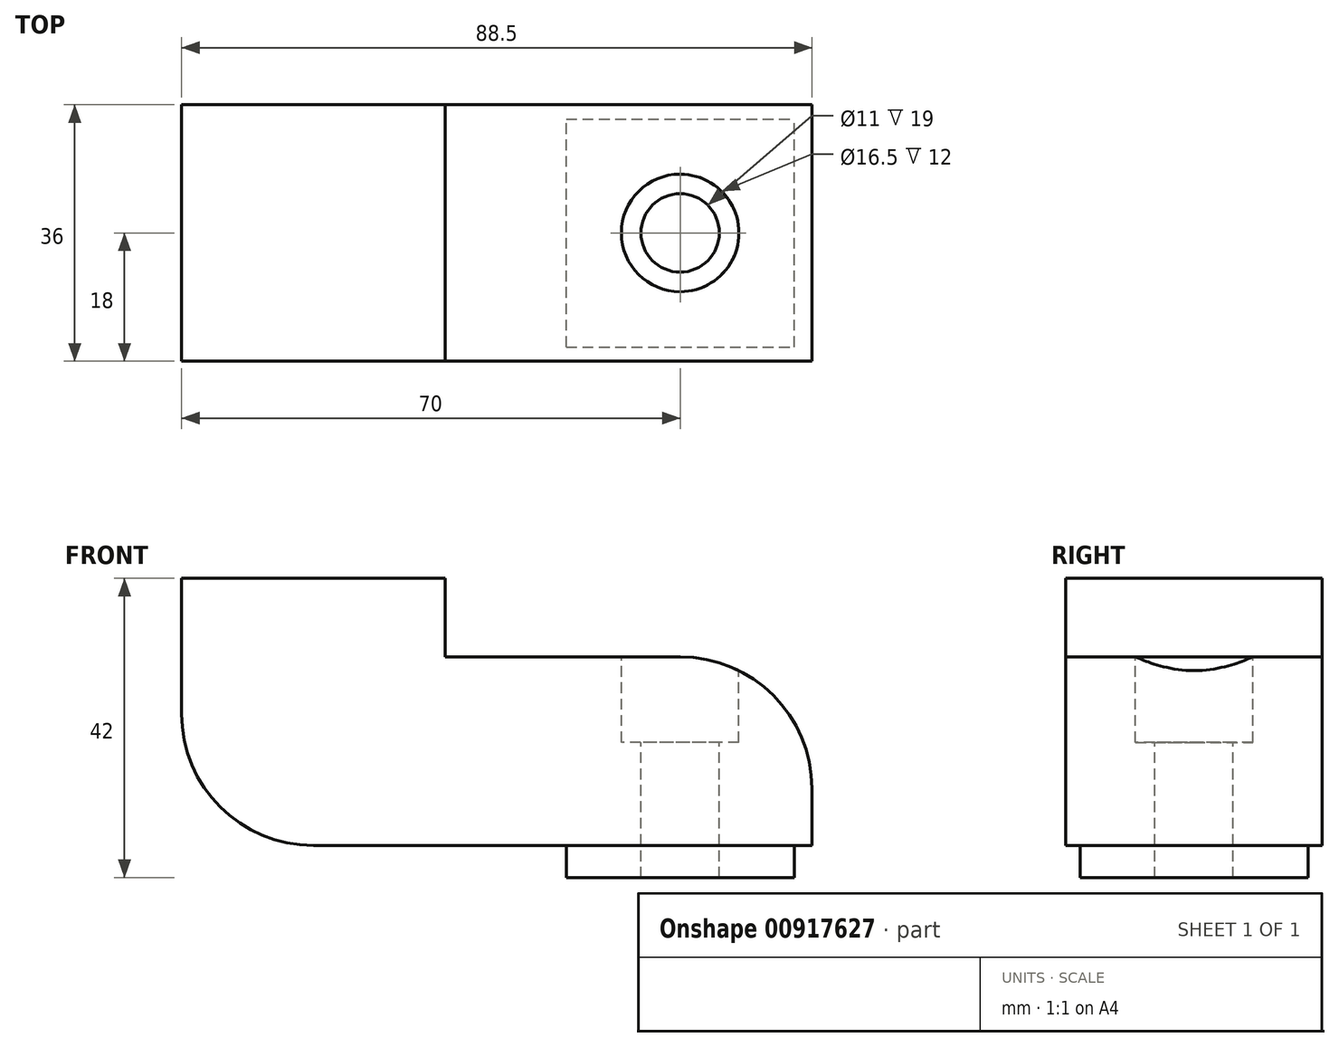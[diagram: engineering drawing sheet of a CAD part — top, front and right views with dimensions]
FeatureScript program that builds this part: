
annotation { "Feature Type Name" : "Feature", "Feature Type Description" : "" }
export const myFeature = defineFeature(function(context is Context, id is Id, definition is map)
    precondition{}
    {
        {
            var Q0;
            Q0=qCreatedBy(makeId("Front.planeOp"),FACE);
            var sketch = newSketch(context, id + "F0", { "sketchPlane" : qUnion([Q0])});
            skLineSegment(sketch, "E0.bottom", {"start": v(44.25, 13.25) * mm, "end": v(-44.25, 13.25) * mm});
            skLineSegment(sketch, "E0.top", {"start": v(44.25, -13.25) * mm, "end": v(-44.25, -13.25) * mm});
            skLineSegment(sketch, "E0.left", {"start": v(44.25, 13.25) * mm, "end": v(44.25, -13.25) * mm});
            skLineSegment(sketch, "E0.right", {"start": v(-44.25, 13.25) * mm, "end": v(-44.25, -13.25) * mm});
            skPoint(sketch, "E0.middle", {"position": v(0, 0) * mm});
            skSolve(sketch);
        }
        {
            var Q0;
            Q0 = qSketchRegion(id + "F0", true);
            extrude(context, id + "F1", {"entities" : qUnion([Q0]), "endBound" : BoundingType.SYMMETRIC, "depth" : 36 * mm, "offsetDistance" : 25 * mm});
        }
        {
            var Q0;
            Q0=makeQuery(id+"F1.opExtrude","SWEPT_FACE",FACE,{"disambiguationData":[OSD([sQuery(id+"F0.wireOp",EDGE,"E0.bottom")])]});
            var sketch = newSketch(context, id + "F2", { "sketchPlane" : qUnion([Q0])});
            skLineSegment(sketch, "E1.bottom", {"start": v(-44.25, 18) * mm, "end": v(-7.25, 18) * mm});
            skLineSegment(sketch, "E1.top", {"start": v(-44.25, -18) * mm, "end": v(-7.25, -18) * mm});
            skLineSegment(sketch, "E1.left", {"start": v(-44.25, 18) * mm, "end": v(-44.25, -18) * mm});
            skLineSegment(sketch, "E1.right", {"start": v(-7.25, 18) * mm, "end": v(-7.25, -18) * mm});
            skSolve(sketch);
        }
        {
            var Q0;
            Q0 = qSketchRegion(id + "F2", true);
            extrude(context, id + "F3", {"entities" : qUnion([Q0]), "operationType" : NewBodyOperationType.ADD, "depth" : 11 * mm, "offsetDistance" : 25 * mm});
        }
        {
            var Q0;
            Q0=makeQuery(id+"F1.opExtrude","SWEPT_EDGE",EDGE,{"disambiguationData":[OSD([sQuery(id+"F0.wireOp",EDGE,"E0.bottom"),sQuery(id+"F0.wireOp",EDGE,"E0.left")])]});
            var Q1;
            Q1=makeQuery(id+"F1.opExtrude","SWEPT_EDGE",EDGE,{"disambiguationData":[OSD([sQuery(id+"F0.wireOp",EDGE,"E0.top"),sQuery(id+"F0.wireOp",EDGE,"E0.right")])]});
            fillet(context, id + "F4", {"entities" : qUnion([Q0, Q1]), "radius" : 18.5 * mm, "tangentPropagation" : true, "allowEdgeOverflow" : false});
        }
        {
            var Q0;
            Q0=makeQuery(id+"F1.opExtrude","SWEPT_FACE",FACE,{"disambiguationData":[OSD([sQuery(id+"F0.wireOp",EDGE,"E0.bottom")])]});
            var sketch = newSketch(context, id + "F5", { "sketchPlane" : qUnion([Q0])});
            skPoint(sketch, "E2", {"position": v(25.75, 0) * mm});
            skSolve(sketch);
        }
        {
            var Q0;
            Q0=makeQuery(id+"F1.opExtrude","SWEPT_FACE",FACE,{"disambiguationData":[OSD([sQuery(id+"F0.wireOp",EDGE,"E0.top")])]});
            var sketch = newSketch(context, id + "F6", { "sketchPlane" : qUnion([Q0])});
            skLineSegment(sketch, "E3.bottom", {"start": v(9.75, 16) * mm, "end": v(41.75, 16) * mm});
            skLineSegment(sketch, "E3.top", {"start": v(9.75, -16) * mm, "end": v(41.75, -16) * mm});
            skLineSegment(sketch, "E3.left", {"start": v(9.75, 16) * mm, "end": v(9.75, -16) * mm});
            skLineSegment(sketch, "E3.right", {"start": v(41.75, 16) * mm, "end": v(41.75, -16) * mm});
            skSolve(sketch);
        }
        {
            var Q0;
            Q0 = qSketchRegion(id + "F6", true);
            extrude(context, id + "F7", {"entities" : qUnion([Q0]), "operationType" : NewBodyOperationType.ADD, "depth" : 4.5 * mm, "offsetDistance" : 25 * mm});
        }
        {
            var Q0;
            Q0=sQuery(id+"F5.wireOp",VERTEX,"E2");
            var Q1;
            Q1=makeQuery(id+"F1.opExtrude","SWEPT_BODY",BODY,{"disambiguationData":[OSD([sQuery(id+"F0.wireOp",EDGE,"E0.bottom"),sQuery(id+"F0.wireOp",EDGE,"E0.top"),sQuery(id+"F0.wireOp",EDGE,"E0.left"),sQuery(id+"F0.wireOp",EDGE,"E0.right")])]});
            hole(context, id + "F8", {"style" : HoleStyle.C_BORE, "endStyle" : HoleEndStyle.THROUGH, "holeDiameter" : 11 * mm, "cBoreDiameter" : 16.5 * mm, "cBoreDepth" : 12 * mm, "majorDiameter" : 5 * mm, "isTappedThrough" : true, "tappedDepth" : 12 * mm, "tapClearance" : 3, "startFromSketch" : true, "locations" : qUnion([Q0]), "scope" : qUnion([Q1])});
        }
    });
